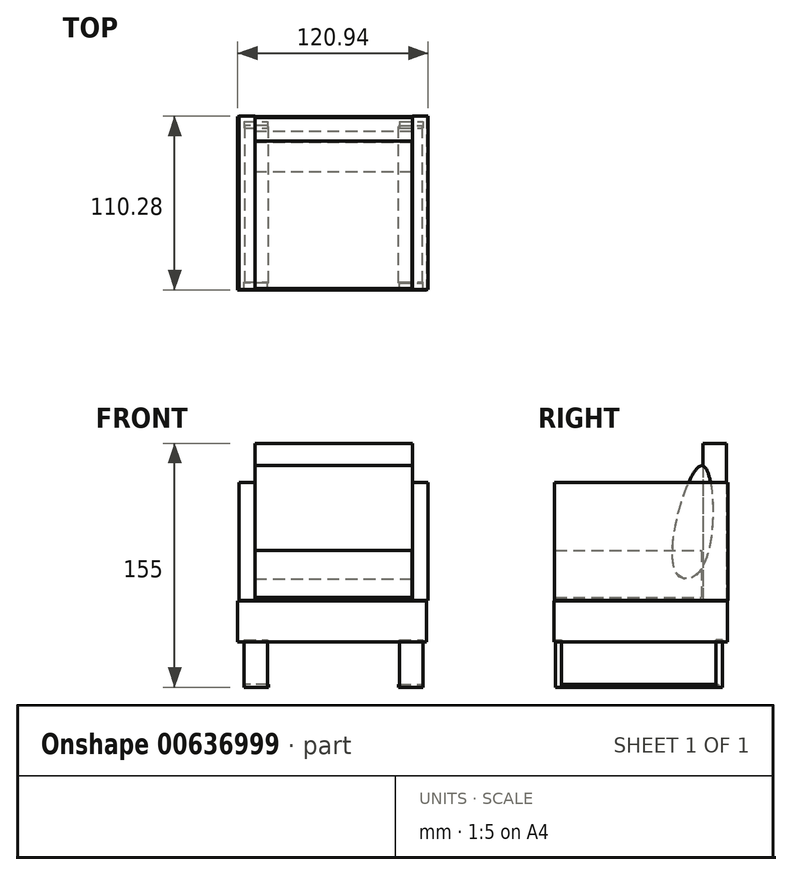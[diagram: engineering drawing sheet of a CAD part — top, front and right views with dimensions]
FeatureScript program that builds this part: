
annotation { "Feature Type Name" : "Feature", "Feature Type Description" : "" }
export const myFeature = defineFeature(function(context is Context, id is Id, definition is map)
    precondition{}
    {
        {
            var Q0;
            Q0=qCreatedBy(makeId("Top.planeOp"),FACE);
            var sketch = newSketch(context, id + "F0", { "sketchPlane" : qUnion([Q0])});
            skLineSegment(sketch, "E0.bottom", {"start": v(-41.27, -49.45) * mm, "end": v(-56.27, -49.45) * mm});
            skLineSegment(sketch, "E0.top", {"start": v(-41.27, 50.55) * mm, "end": v(-56.27, 50.55) * mm});
            skLineSegment(sketch, "E0.left", {"start": v(-41.27, -49.45) * mm, "end": v(-41.27, 50.55) * mm});
            skLineSegment(sketch, "E0.right", {"start": v(-56.27, -49.45) * mm, "end": v(-56.27, 50.55) * mm});
            skSolve(sketch);
        }
        {
            var Q0;
            Q0=makeQuery(id+"F0.imprint","IMPRINT",FACE,{"disambiguationData":[TD([[makeQuery(id+"F0.imprint","IMPRINT",EDGE,{"derivedFrom":sQuery(id+"F0.wireOp",EDGE,"E0.bottom")}),-1.0]])]});
            extrude(context, id + "F1", {"entities" : qUnion([Q0]), "depth" : 2 * mm, "offsetDistance" : 25 * mm});
        }
        {
            var Q0;
            Q0=makeQuery(id+"F1.opExtrude","SWEPT_BODY",BODY,{"disambiguationData":[OSD([sQuery(id+"F0.wireOp",EDGE,"E0.bottom"),sQuery(id+"F0.wireOp",EDGE,"E0.top"),sQuery(id+"F0.wireOp",EDGE,"E0.left"),sQuery(id+"F0.wireOp",EDGE,"E0.right")])]});
            var Q1;
            Q1=qCreatedBy(makeId("Right.planeOp"),FACE);
            mirror(context, id + "F2", {"entities" : qUnion([Q0]), "mirrorPlane" : qUnion([Q1])});
        }
        {
            var Q0;
            Q0=qCreatedBy(makeId("Front.planeOp"),FACE);
            cPlane(context, id + "F3", {"entities" : qUnion([Q0]), "cplaneType" : CPlaneType.OFFSET, "offset" : 50 * mm, "width" : 150 * mm, "height" : 150 * mm});
        }
        {
            var Q0;
            Q0=qCreatedBy(id+"F3.planeOp",FACE);
            var sketch = newSketch(context, id + "F4", { "sketchPlane" : qUnion([Q0])});
            skLineSegment(sketch, "E1.bottom", {"start": v(-56.9, 30) * mm, "end": v(-41.9, 30) * mm});
            skLineSegment(sketch, "E1.top", {"start": v(-56.9, 0) * mm, "end": v(-41.9, 0) * mm});
            skLineSegment(sketch, "E1.left", {"start": v(-56.9, 30) * mm, "end": v(-56.9, 0) * mm});
            skLineSegment(sketch, "E1.right", {"start": v(-41.9, 30) * mm, "end": v(-41.9, 0) * mm});
            skLineSegment(sketch, "E2.bottom", {"start": v(41.7, 0) * mm, "end": v(56.7, 0) * mm});
            skLineSegment(sketch, "E2.top", {"start": v(41.7, 30) * mm, "end": v(56.7, 30) * mm});
            skLineSegment(sketch, "E2.left", {"start": v(41.7, 0) * mm, "end": v(41.7, 30) * mm});
            skLineSegment(sketch, "E2.right", {"start": v(56.7, 0) * mm, "end": v(56.7, 30) * mm});
            skSolve(sketch);
        }
        {
            var Q0;
            Q0 = qSketchRegion(id + "F4", true);
            extrude(context, id + "F5", {"entities" : qUnion([Q0]), "depth" : 3 * mm, "offsetDistance" : 25 * mm, "hasSecondDirection" : true, "secondDirectionOppositeDirection" : true, "secondDirectionDepth" : 1 * mm});
        }
        {
            var Q0;
            Q0=makeQuery(id+"F5.opExtrude","SWEPT_BODY",BODY,{"disambiguationData":[OSD([sQuery(id+"F4.wireOp",EDGE,"E1.bottom"),sQuery(id+"F4.wireOp",EDGE,"E1.top"),sQuery(id+"F4.wireOp",EDGE,"E1.left"),sQuery(id+"F4.wireOp",EDGE,"E1.right")])]});
            var Q1;
            Q1=makeQuery(id+"F5.opExtrude","SWEPT_BODY",BODY,{"disambiguationData":[OSD([sQuery(id+"F4.wireOp",EDGE,"E2.bottom"),sQuery(id+"F4.wireOp",EDGE,"E2.top"),sQuery(id+"F4.wireOp",EDGE,"E2.left"),sQuery(id+"F4.wireOp",EDGE,"E2.right")])]});
            var Q2;
            Q2=qCreatedBy(makeId("Front.planeOp"),FACE);
            mirror(context, id + "F6", {"entities" : qUnion([Q0, Q1]), "mirrorPlane" : qUnion([Q2])});
        }
        {
            var Q0;
            Q0=qCreatedBy(makeId("Top.planeOp"),FACE);
            cPlane(context, id + "F7", {"entities" : qUnion([Q0]), "cplaneType" : CPlaneType.OFFSET, "offset" : 30 * mm, "width" : 150 * mm, "height" : 150 * mm});
        }
        {
            var Q0;
            Q0=qCreatedBy(id+"F7.planeOp",FACE);
            var sketch = newSketch(context, id + "F8", { "sketchPlane" : qUnion([Q0])});
            skLineSegment(sketch, "E3.bottom", {"start": v(-60.94, 56.2) * mm, "end": v(59.06, 56.2) * mm});
            skLineSegment(sketch, "E3.top", {"start": v(-60.94, -53.8) * mm, "end": v(59.06, -53.8) * mm});
            skLineSegment(sketch, "E3.left", {"start": v(-60.94, 56.2) * mm, "end": v(-60.94, -53.8) * mm});
            skLineSegment(sketch, "E3.right", {"start": v(59.06, 56.2) * mm, "end": v(59.06, -53.8) * mm});
            skSolve(sketch);
        }
        {
            var Q0;
            Q0=makeQuery(id+"F8.imprint","IMPRINT",FACE,{"disambiguationData":[TD([[makeQuery(id+"F8.imprint","IMPRINT",EDGE,{"derivedFrom":sQuery(id+"F8.wireOp",EDGE,"E3.bottom")}),-1.0]])]});
            extrude(context, id + "F9", {"entities" : qUnion([Q0]), "depth" : 25 * mm, "offsetDistance" : 25 * mm, "hasSecondDirection" : true, "secondDirectionOppositeDirection" : true, "secondDirectionDepth" : 1 * mm});
        }
        {
            var Q0;
            Q0=qCreatedBy(makeId("Right.planeOp"),FACE);
            cPlane(context, id + "F10", {"entities" : qUnion([Q0]), "cplaneType" : CPlaneType.OFFSET, "offset" : 50 * mm, "width" : 150 * mm, "height" : 150 * mm});
        }
        {
            var Q0;
            Q0=qCreatedBy(id+"F10.planeOp",FACE);
            var sketch = newSketch(context, id + "F11", { "sketchPlane" : qUnion([Q0])});
            skLineSegment(sketch, "E4.bottom", {"start": v(-53.5, 55.23) * mm, "end": v(56.5, 55.23) * mm});
            skLineSegment(sketch, "E4.top", {"start": v(-53.5, 130.23) * mm, "end": v(56.5, 130.23) * mm});
            skLineSegment(sketch, "E4.left", {"start": v(-53.5, 55.23) * mm, "end": v(-53.5, 130.23) * mm});
            skLineSegment(sketch, "E4.right", {"start": v(56.5, 55.23) * mm, "end": v(56.5, 130.23) * mm});
            skSolve(sketch);
        }
        {
            var Q0;
            Q0=makeQuery(id+"F11.imprint","IMPRINT",FACE,{"disambiguationData":[TD([[makeQuery(id+"F11.imprint","IMPRINT",EDGE,{"derivedFrom":sQuery(id+"F11.wireOp",EDGE,"E4.bottom")}),1.0]])]});
            extrude(context, id + "F12", {"entities" : qUnion([Q0]), "depth" : 10 * mm, "offsetDistance" : 25 * mm});
        }
        {
            var Q0;
            Q0=makeQuery(id+"F12.opExtrude","SWEPT_BODY",BODY,{"disambiguationData":[OSD([sQuery(id+"F11.wireOp",EDGE,"E4.bottom"),sQuery(id+"F11.wireOp",EDGE,"E4.top"),sQuery(id+"F11.wireOp",EDGE,"E4.left"),sQuery(id+"F11.wireOp",EDGE,"E4.right")])]});
            var Q1;
            Q1=qCreatedBy(makeId("Right.planeOp"),FACE);
            mirror(context, id + "F13", {"entities" : qUnion([Q0]), "mirrorPlane" : qUnion([Q1])});
        }
        {
            var Q0;
            Q0=qCreatedBy(id+"F7.planeOp",FACE);
            cPlane(context, id + "F14", {"entities" : qUnion([Q0]), "cplaneType" : CPlaneType.OFFSET, "offset" : 25 * mm, "width" : 150 * mm, "height" : 150 * mm});
        }
        {
            var Q0;
            Q0=qCreatedBy(id+"F14.planeOp",FACE);
            var sketch = newSketch(context, id + "F15", { "sketchPlane" : qUnion([Q0])});
            skLineSegment(sketch, "E5.bottom", {"start": v(-50.03, 55.68) * mm, "end": v(49.97, 55.68) * mm});
            skLineSegment(sketch, "E5.top", {"start": v(-50.03, 40.68) * mm, "end": v(49.97, 40.68) * mm});
            skLineSegment(sketch, "E5.left", {"start": v(-50.03, 55.68) * mm, "end": v(-50.03, 40.68) * mm});
            skLineSegment(sketch, "E5.right", {"start": v(49.97, 55.68) * mm, "end": v(49.97, 40.68) * mm});
            skSolve(sketch);
        }
        {
            var Q0;
            Q0 = qSketchRegion(id + "F15", true);
            extrude(context, id + "F16", {"entities" : qUnion([Q0]), "depth" : 100 * mm, "offsetDistance" : 25 * mm});
        }
        {
            var Q0;
            Q0=qCreatedBy(id+"F14.planeOp",FACE);
            cPlane(context, id + "F17", {"entities" : qUnion([Q0]), "cplaneType" : CPlaneType.OFFSET, "offset" : 2 * mm, "width" : 150 * mm, "height" : 150 * mm});
        }
        {
            var Q0;
            Q0=qCreatedBy(id+"F17.planeOp",FACE);
            var sketch = newSketch(context, id + "F18", { "sketchPlane" : qUnion([Q0])});
            skLineSegment(sketch, "E6.bottom", {"start": v(-50.28, -53.08) * mm, "end": v(49.72, -53.08) * mm});
            skLineSegment(sketch, "E6.top", {"start": v(-50.28, 39.92) * mm, "end": v(49.72, 39.92) * mm});
            skLineSegment(sketch, "E6.left", {"start": v(-50.28, -53.08) * mm, "end": v(-50.28, 39.92) * mm});
            skLineSegment(sketch, "E6.right", {"start": v(49.72, -53.08) * mm, "end": v(49.72, 39.92) * mm});
            skSolve(sketch);
        }
        {
            var Q0;
            Q0 = qSketchRegion(id + "F18", true);
            extrude(context, id + "F19", {"entities" : qUnion([Q0]), "operationType" : NewBodyOperationType.ADD, "depth" : 30 * mm, "offsetDistance" : 25 * mm});
        }
        {
            var Q0;
            Q0=qCreatedBy(id+"F10.planeOp",FACE);
            var sketch = newSketch(context, id + "F20", { "sketchPlane" : qUnion([Q0])});
            skFitSpline(sketch, "E7", {"points": [v(40.06, 140.78) * mm, v(40.06, 75.55) * mm, v(22.95, 74.48) * mm, v(40.06, 140.78) * mm]});
            skSolve(sketch);
        }
        {
            var Q0;
            Q0=makeQuery(id+"F20.imprint","IMPRINT",FACE,{"disambiguationData":[TD([[makeQuery(id+"F20.imprint","IMPRINT",EDGE,{"derivedFrom":sQuery(id+"F20.wireOp",EDGE,"E7")}),-1.0]])]});
            extrude(context, id + "F21", {"entities" : qUnion([Q0]), "oppositeDirection" : true, "depth" : 100 * mm, "offsetDistance" : 25 * mm});
        }
    });
